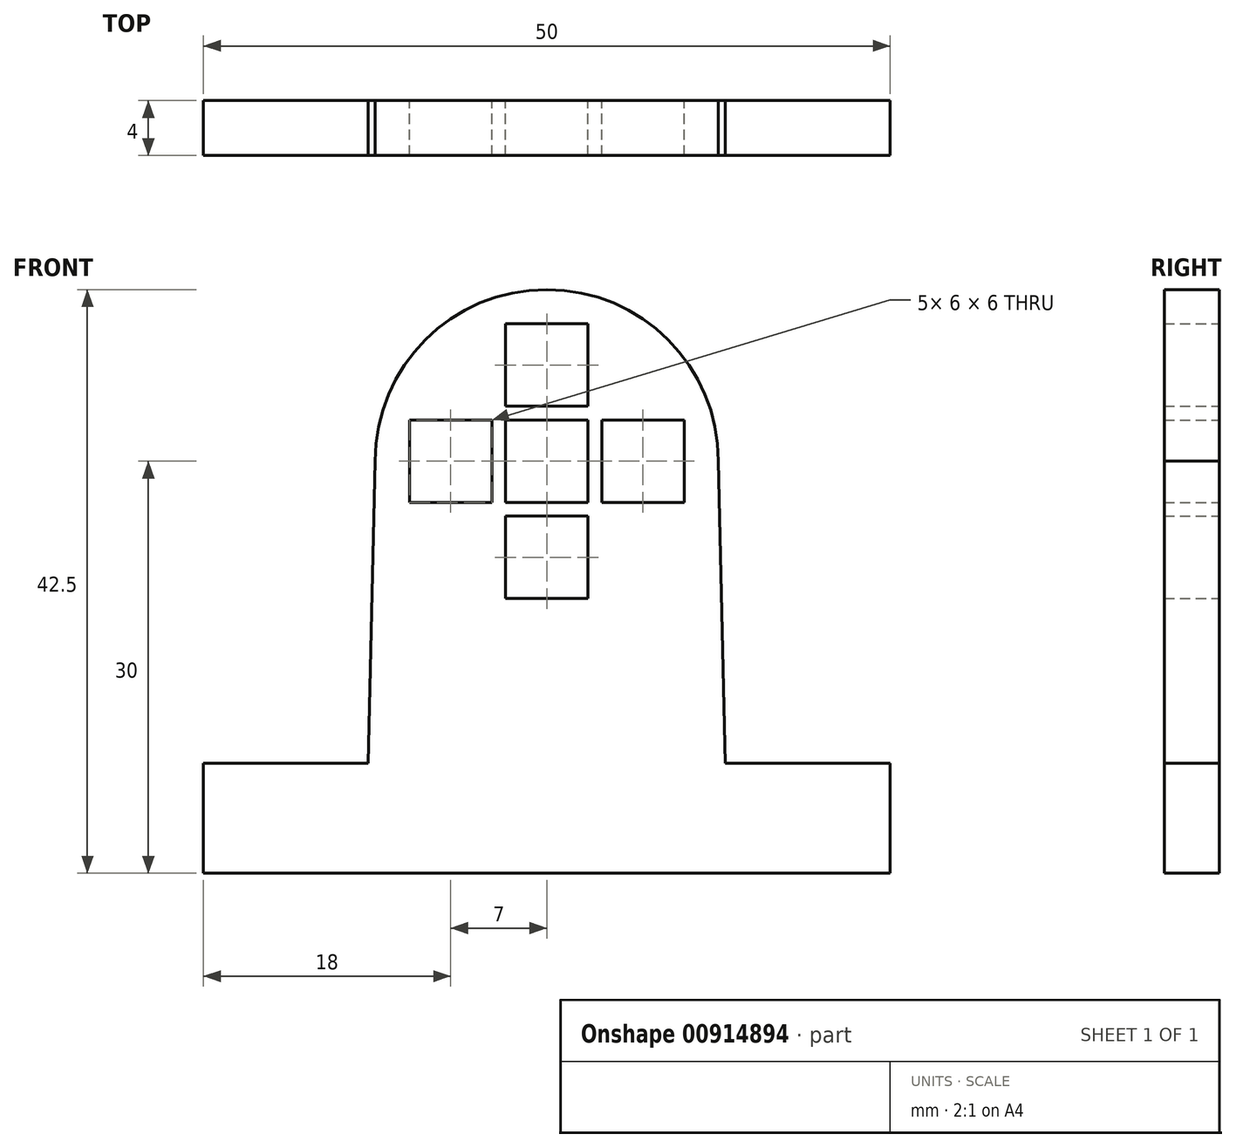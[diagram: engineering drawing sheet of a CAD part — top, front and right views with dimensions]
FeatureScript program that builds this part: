
annotation { "Feature Type Name" : "Feature", "Feature Type Description" : "" }
export const myFeature = defineFeature(function(context is Context, id is Id, definition is map)
    precondition{}
    {
        {
            var Q0;
            Q0=qCreatedBy(makeId("Front.planeOp"),FACE);
            var sketch = newSketch(context, id + "F0", { "sketchPlane" : qUnion([Q0])});
            skCircle(sketch, "E0", {"center": v(0, 0) * mm, "radius": 12.5 * mm});
            skLineSegment(sketch, "E1", {"start": v(0, 13.52) * mm, "end": v(0, -27.91) * mm, "construction": true});
            skLineSegment(sketch, "E2", {"start": v(0, -30) * mm, "end": v(25, -30) * mm});
            skLineSegment(sketch, "E3", {"start": v(25, -30) * mm, "end": v(25, -22) * mm});
            skLineSegment(sketch, "E4", {"start": v(25, -22) * mm, "end": v(13, -22) * mm});
            skLineSegment(sketch, "E5", {"start": v(13, -22) * mm, "end": v(12.5, 0) * mm});
            skLineSegment(sketch, "E6.MirrorCS", {"start": v(-13, -22) * mm, "end": v(-12.5, 0) * mm});
            skLineSegment(sketch, "E7.MirrorCS", {"start": v(-25, -22) * mm, "end": v(-13, -22) * mm});
            skLineSegment(sketch, "E8.MirrorCS", {"start": v(0, -30) * mm, "end": v(-25, -30) * mm});
            skLineSegment(sketch, "E9.MirrorCS", {"start": v(-25, -30) * mm, "end": v(-25, -22) * mm});
            skLineSegment(sketch, "E10", {"start": v(-14.86, 0) * mm, "end": v(15.9, 0) * mm, "construction": true});
            skLineSegment(sketch, "E11.bottom", {"start": v(3, -3) * mm, "end": v(-3, -3) * mm});
            skLineSegment(sketch, "E11.top", {"start": v(3, 3) * mm, "end": v(-3, 3) * mm});
            skLineSegment(sketch, "E11.left", {"start": v(3, -3) * mm, "end": v(3, 3) * mm});
            skLineSegment(sketch, "E11.right", {"start": v(-3, -3) * mm, "end": v(-3, 3) * mm});
            skLineSegment(sketch, "E12.bottom", {"start": v(3, 4) * mm, "end": v(-3, 4) * mm});
            skLineSegment(sketch, "E12.top", {"start": v(3, 10) * mm, "end": v(-3, 10) * mm});
            skLineSegment(sketch, "E12.left", {"start": v(3, 4) * mm, "end": v(3, 10) * mm});
            skLineSegment(sketch, "E12.right", {"start": v(-3, 4) * mm, "end": v(-3, 10) * mm});
            skPoint(sketch, "E12.middle", {"position": v(0, 7) * mm});
            skLineSegment(sketch, "E13.bottom", {"start": v(3, -10) * mm, "end": v(-3, -10) * mm});
            skLineSegment(sketch, "E13.top", {"start": v(3, -4) * mm, "end": v(-3, -4) * mm});
            skLineSegment(sketch, "E13.left", {"start": v(3, -10) * mm, "end": v(3, -4) * mm});
            skLineSegment(sketch, "E13.right", {"start": v(-3, -10) * mm, "end": v(-3, -4) * mm});
            skPoint(sketch, "E13.middle", {"position": v(0, -7) * mm});
            skLineSegment(sketch, "E14.bottom", {"start": v(-4, -3) * mm, "end": v(-10, -3) * mm});
            skLineSegment(sketch, "E14.top", {"start": v(-4, 3) * mm, "end": v(-10, 3) * mm});
            skLineSegment(sketch, "E14.left", {"start": v(-4, -3) * mm, "end": v(-4, 3) * mm});
            skLineSegment(sketch, "E14.right", {"start": v(-10, -3) * mm, "end": v(-10, 3) * mm});
            skPoint(sketch, "E14.middle", {"position": v(-7, 0) * mm});
            skLineSegment(sketch, "E15.bottom", {"start": v(4, -3) * mm, "end": v(10, -3) * mm});
            skLineSegment(sketch, "E15.top", {"start": v(4, 3) * mm, "end": v(10, 3) * mm});
            skLineSegment(sketch, "E15.left", {"start": v(4, -3) * mm, "end": v(4, 3) * mm});
            skLineSegment(sketch, "E15.right", {"start": v(10, -3) * mm, "end": v(10, 3) * mm});
            skPoint(sketch, "E15.middle", {"position": v(7, 0) * mm});
            skSolve(sketch);
        }
        {
            var Q0;
            Q0 = qSketchRegion(id + "F0", true);
            extrude(context, id + "F1", {"entities" : qUnion([Q0]), "depth" : 4 * mm, "offsetDistance" : 25 * mm});
        }
    });
